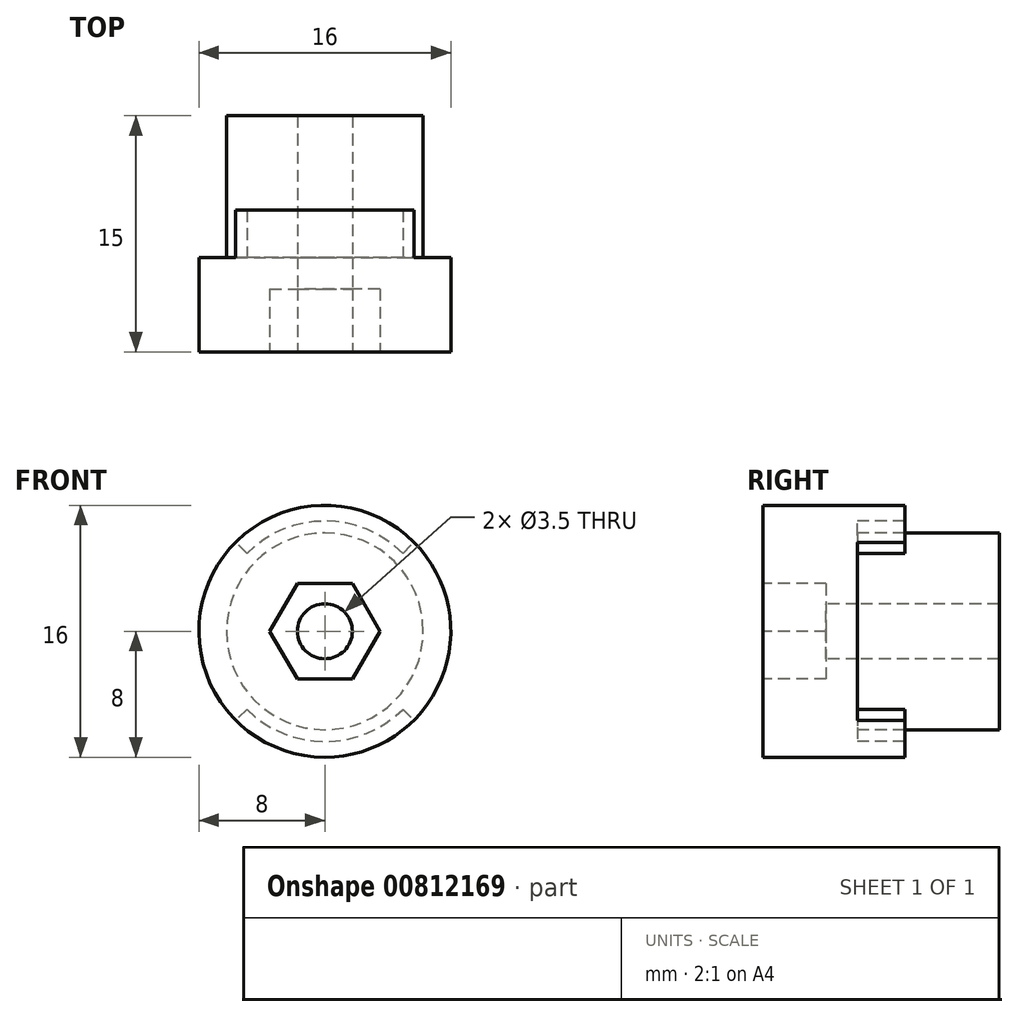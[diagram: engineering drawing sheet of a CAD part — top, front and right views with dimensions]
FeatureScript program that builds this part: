
annotation { "Feature Type Name" : "Feature", "Feature Type Description" : "" }
export const myFeature = defineFeature(function(context is Context, id is Id, definition is map)
    precondition{}
    {
        {
            var Q0;
            Q0=qCreatedBy(makeId("Front.planeOp"),FACE);
            var sketch = newSketch(context, id + "F0", { "sketchPlane" : qUnion([Q0])});
            skCircle(sketch, "E0", {"center": v(0, 0) * mm, "radius": 8 * mm});
            skSolve(sketch);
        }
        {
            var Q0;
            Q0=makeQuery(id+"F0.imprint","IMPRINT",FACE,{"disambiguationData":[TD([[makeQuery(id+"F0.imprint","IMPRINT",EDGE,{"derivedFrom":sQuery(id+"F0.wireOp",EDGE,"E0")}),1.0]])]});
            extrude(context, id + "F1", {"entities" : qUnion([Q0]), "depth" : 6 * mm, "offsetDistance" : 25 * mm});
        }
        {
            var Q0;
            Q0=makeQuery(id+"F1.opExtrude","CAP_FACE",FACE,{"disambiguationData":[OSD([sQuery(id+"F0.wireOp",EDGE,"E0")])],"isStart":false});
            var sketch = newSketch(context, id + "F2", { "sketchPlane" : qUnion([Q0])});
            skCircle(sketch, "E1.cCircle", {"center": v(0, 0) * mm, "radius": 3.5 * mm, "construction": true});
            skLineSegment(sketch, "E1.0", {"start": v(1.75, -3.03) * mm, "end": v(-1.75, -3.03) * mm});
            skLineSegment(sketch, "E1.1", {"start": v(-1.75, -3.03) * mm, "end": v(-3.5, 0) * mm});
            skLineSegment(sketch, "E1.2", {"start": v(-3.5, 0) * mm, "end": v(-1.75, 3.03) * mm});
            skLineSegment(sketch, "E1.3", {"start": v(-1.75, 3.03) * mm, "end": v(1.75, 3.03) * mm});
            skLineSegment(sketch, "E1.4", {"start": v(1.75, 3.03) * mm, "end": v(3.5, 0) * mm});
            skLineSegment(sketch, "E1.5", {"start": v(3.5, 0) * mm, "end": v(1.75, -3.03) * mm});
            skSolve(sketch);
        }
        {
            var Q0;
            Q0=makeQuery(id+"F2.imprint","IMPRINT",FACE,{"disambiguationData":[TD([[makeQuery(id+"F2.imprint","IMPRINT",EDGE,{"derivedFrom":sQuery(id+"F2.wireOp",EDGE,"E1.0")}),-1.0]])]});
            extrude(context, id + "F3", {"entities" : qUnion([Q0]), "operationType" : NewBodyOperationType.REMOVE, "oppositeDirection" : true, "depth" : 4 * mm, "offsetDistance" : 25 * mm});
        }
        {
            var Q0;
            Q0=makeQuery(id+"F1.opExtrude","CAP_FACE",FACE,{"disambiguationData":[OSD([sQuery(id+"F0.wireOp",EDGE,"E0")])],"isStart":true});
            var sketch = newSketch(context, id + "F4", { "sketchPlane" : qUnion([Q0])});
            skArc(sketch, "E2", {"start": v(5.66, 5.66) * mm, "mid": v(0, 8) * mm, "end": v(-5.66, 5.66) * mm});
            skLineSegment(sketch, "E3", {"start": v(4.95, 4.95) * mm, "end": v(5.66, 5.66) * mm});
            skLineSegment(sketch, "E4", {"start": v(-4.95, -4.95) * mm, "end": v(-5.66, -5.66) * mm});
            skLineSegment(sketch, "E5", {"start": v(-4.95, 4.95) * mm, "end": v(-5.66, 5.66) * mm});
            skLineSegment(sketch, "E6", {"start": v(4.95, -4.95) * mm, "end": v(5.66, -5.66) * mm});
            skLineSegment(sketch, "E7", {"start": v(0, 0) * mm, "end": v(0, 9.02) * mm, "construction": true});
            skLineSegment(sketch, "E8", {"start": v(0, 0) * mm, "end": v(0, -9.39) * mm, "construction": true});
            skArc(sketch, "E9", {"start": v(4.95, 4.95) * mm, "mid": v(0, 7) * mm, "end": v(-4.95, 4.95) * mm});
            skArc(sketch, "E10.trimOffspring", {"start": v(-4.95, -4.95) * mm, "mid": v(0, -7) * mm, "end": v(4.95, -4.95) * mm});
            skArc(sketch, "E11.trimOffspring", {"start": v(-5.66, -5.66) * mm, "mid": v(0, -8) * mm, "end": v(5.66, -5.66) * mm});
            skSolve(sketch);
        }
        {
            var Q0;
            Q0=makeQuery(id+"F4.imprint","IMPRINT",FACE,{"disambiguationData":[TD([[makeQuery(id+"F4.imprint","IMPRINT",EDGE,{"derivedFrom":sQuery(id+"F4.wireOp",EDGE,"E4")}),1.0]])]});
            var Q1;
            Q1=makeQuery(id+"F4.imprint","IMPRINT",FACE,{"disambiguationData":[TD([[makeQuery(id+"F4.imprint","IMPRINT",EDGE,{"derivedFrom":sQuery(id+"F4.wireOp",EDGE,"E2")}),-1.0]])]});
            extrude(context, id + "F5", {"entities" : qUnion([Q0, Q1]), "operationType" : NewBodyOperationType.ADD, "depth" : 3 * mm, "offsetDistance" : 25 * mm});
        }
        {
            var Q0;
            Q0=makeQuery(id+"F3.boolean.opBoolean","COPY",FACE,{"derivedFrom":makeQuery(id+"F3.opExtrude","CAP_FACE",FACE,{"disambiguationData":[OSD([sQuery(id+"F2.wireOp",EDGE,"E1.0"),sQuery(id+"F2.wireOp",EDGE,"E1.1"),sQuery(id+"F2.wireOp",EDGE,"E1.2"),sQuery(id+"F2.wireOp",EDGE,"E1.3"),sQuery(id+"F2.wireOp",EDGE,"E1.4"),sQuery(id+"F2.wireOp",EDGE,"E1.5")])],"isStart":false})});
            var sketch = newSketch(context, id + "F6", { "sketchPlane" : qUnion([Q0])});
            skCircle(sketch, "E12", {"center": v(0, 0) * mm, "radius": 1.75 * mm});
            skSolve(sketch);
        }
        {
            var Q0;
            Q0=makeQuery(id+"F6.imprint","IMPRINT",FACE,{"disambiguationData":[TD([[makeQuery(id+"F6.imprint","IMPRINT",EDGE,{"derivedFrom":sQuery(id+"F6.wireOp",EDGE,"E12")}),1.0]])]});
            extrude(context, id + "F7", {"entities" : qUnion([Q0]), "operationType" : NewBodyOperationType.REMOVE, "oppositeDirection" : true, "depth" : 25 * mm, "offsetDistance" : 25 * mm});
        }
        {
            var Q0;
            Q0=makeQuery(id+"F1.opExtrude","CAP_FACE",FACE,{"disambiguationData":[OSD([sQuery(id+"F0.wireOp",EDGE,"E0")])],"isStart":true});
            var sketch = newSketch(context, id + "F8", { "sketchPlane" : qUnion([Q0])});
            skCircle(sketch, "E13", {"center": v(0, 0) * mm, "radius": 6.25 * mm});
            skSolve(sketch);
        }
        {
            var Q0;
            Q0=makeQuery(id+"F8.imprint","IMPRINT",FACE,{"disambiguationData":[TD([[makeQuery(id+"F8.imprint","IMPRINT",EDGE,{"derivedFrom":sQuery(id+"F8.wireOp",EDGE,"E13")}),1.0]])]});
            extrude(context, id + "F9", {"entities" : qUnion([Q0]), "depth" : 9 * mm, "offsetDistance" : 25 * mm});
        }
    });
